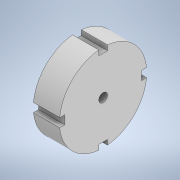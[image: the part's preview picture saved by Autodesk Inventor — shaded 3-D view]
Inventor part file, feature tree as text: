
AUTODESK INVENTOR PART (.ipt)
format: ipt  version: 2022 (Build 260153000, 153)  size: 131,072 bytes
history: native  units: mm
features: sketch x2, other x1, revolve x1, extrude x1
ambient origin geometry x8: Origin, YZ Plane, XZ Plane, XY Plane, X Axis, Y Axis, Z Axis, Center Point
bodies: Body1 (feature_tree)
feature tree (5):
  other  "Твердое тело1"
  revolve  "Вращение1"
  extrude  "Выдавливание1"  Depth=15.0mm
  sketch  "Эскиз1"
  sketch  "Эскиз2"
